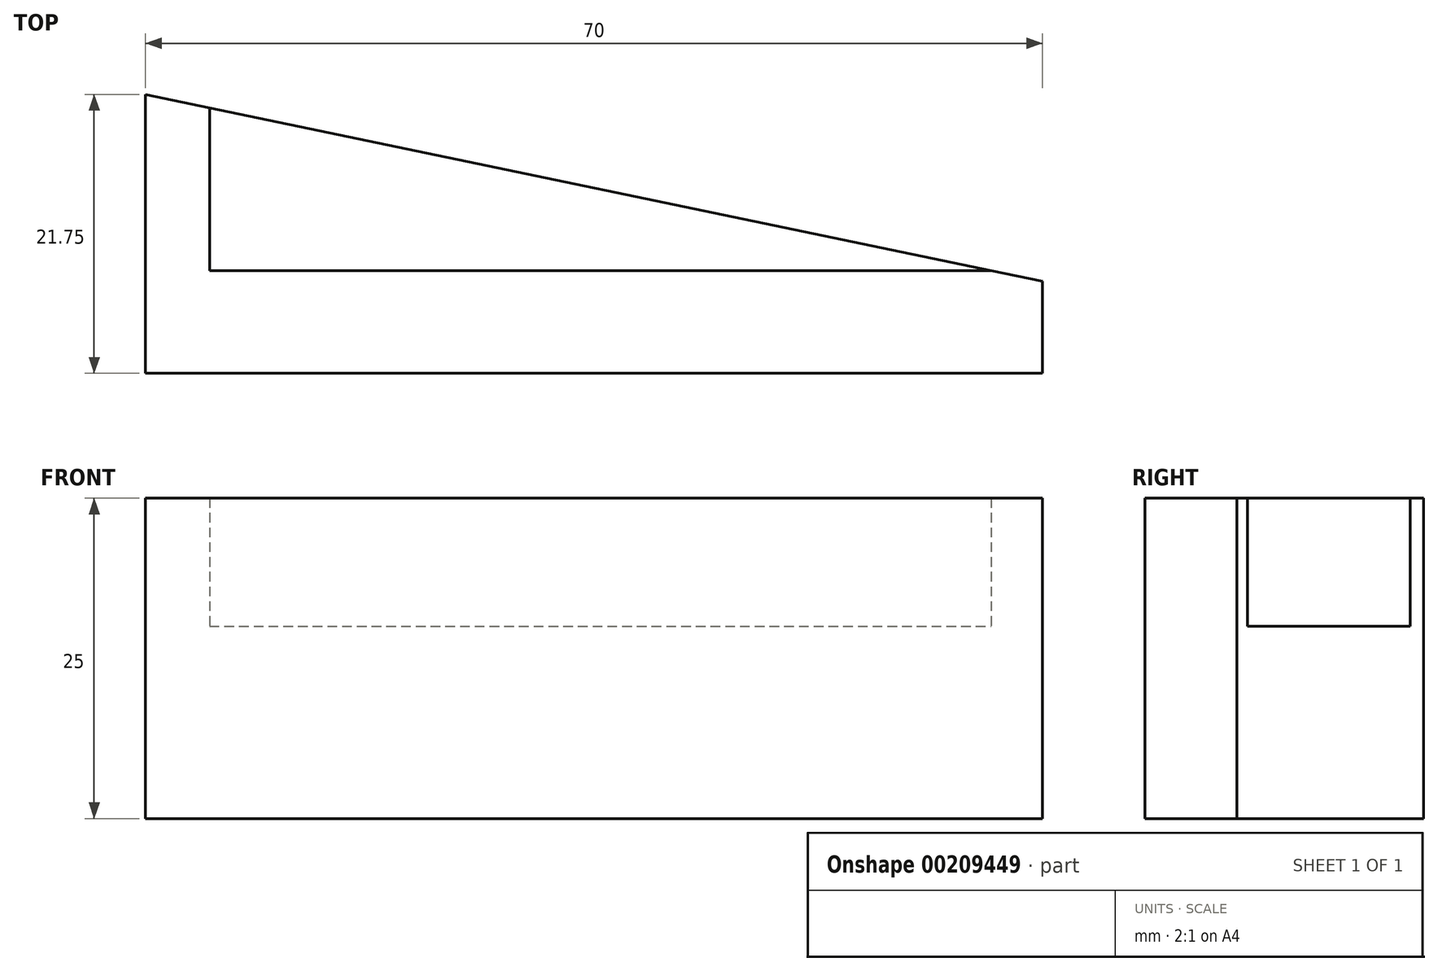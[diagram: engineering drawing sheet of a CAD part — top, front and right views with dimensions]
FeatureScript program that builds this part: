
annotation { "Feature Type Name" : "Feature", "Feature Type Description" : "" }
export const myFeature = defineFeature(function(context is Context, id is Id, definition is map)
    precondition{}
    {
        {
            var Q0;
            Q0=qCreatedBy(makeId("Top.planeOp"),FACE);
            var sketch = newSketch(context, id + "F0", { "sketchPlane" : qUnion([Q0])});
            skLineSegment(sketch, "E0", {"start": v(0, 0) * mm, "end": v(60, 0) * mm});
            skLineSegment(sketch, "E1", {"start": v(60, 0) * mm, "end": v(90, 0) * mm});
            skLineSegment(sketch, "E2", {"start": v(90, 0) * mm, "end": v(90, 18.75) * mm});
            skLineSegment(sketch, "E3", {"start": v(60, 0) * mm, "end": v(60, 12.5) * mm});
            skLineSegment(sketch, "E4", {"start": v(0, 0) * mm, "end": v(90, 18.75) * mm});
            skSolve(sketch);
        }
        {
            var Q0;
            Q0=qSketchRegion(id+"F0",true);
            extrude(context, id + "F1", {"entities" : qUnion([Q0]), "depth" : 15 * mm});
        }
        {
            var Q0;
            Q0=makeQuery(id+"F1.opExtrude","CAP_FACE",FACE,{"disambiguationData":[OSD([sQuery(id+"F0.wireOp",EDGE,"E0"),sQuery(id+"F0.wireOp",EDGE,"HZKhCLW9-oDJk-jZ79-Cc5a-FlSk4M4CYGuW"),sQuery(id+"F0.wireOp",EDGE,"E1"),sQuery(id+"F0.wireOp",EDGE,"E2")])],"isStart":false});
            var sketch = newSketch(context, id + "F2", { "sketchPlane" : qUnion([Q0])});
            skLineSegment(sketch, "E5", {"start": v(90, 0) * mm, "end": v(90, 0) * mm});
            skLineSegment(sketch, "E6", {"start": v(90, 0) * mm, "end": v(0, 0) * mm});
            skLineSegment(sketch, "E7", {"start": v(90, 0) * mm, "end": v(90, 18.75) * mm});
            skLineSegment(sketch, "E8", {"start": v(90, 18.75) * mm, "end": v(85, 17.7) * mm});
            skLineSegment(sketch, "E9.0", {"start": v(85, 5) * mm, "end": v(85, 17.7) * mm});
            skLineSegment(sketch, "E10.0", {"start": v(85, 5) * mm, "end": v(24, 5) * mm});
            skLineSegment(sketch, "E11.trimOffspring", {"start": v(24, 5) * mm, "end": v(0, 0) * mm});
            skSolve(sketch);
        }
        {
            var Q0;
            Q0=qSketchRegion(id+"F2",true);
            extrude(context, id + "F3", {"entities" : qUnion([Q0]), "operationType" : NewBodyOperationType.ADD, "depth" : 10 * mm});
        }
        {
            var Q0;
            Q0=makeQuery(id+"F1.opExtrude","SWEPT_BODY",BODY,{"disambiguationData":[OSD([sQuery(id+"F0.wireOp",EDGE,"E0"),sQuery(id+"F0.wireOp",EDGE,"E1"),sQuery(id+"F0.wireOp",EDGE,"E2"),sQuery(id+"F0.wireOp",EDGE,"E4")])]});
            var Q1;
            Q1=qCreatedBy(makeId("Right.planeOp"),FACE);
            mirror(context, id + "F4", {"entities" : qUnion([Q0]), "mirrorPlane" : qUnion([Q1])});
        }
        {
            var Q0;
            Q0=makeQuery(id+"F1.opExtrude","SWEPT_BODY",BODY,{"disambiguationData":[OSD([sQuery(id+"F0.wireOp",EDGE,"E0"),sQuery(id+"F0.wireOp",EDGE,"E1"),sQuery(id+"F0.wireOp",EDGE,"E2"),sQuery(id+"F0.wireOp",EDGE,"E4")])]});
            deleteBodies(context, id + "F5", {"entities" : qUnion([Q0])});
        }
        {
            var Q0;
            Q0=makeQuery(id+"F4.opPattern","COPY",FACE,{"derivedFrom":makeQuery(id+"F3.boolean.opBoolean","MERGE",FACE,{"derivedFrom":[makeQuery(id+"F1.opExtrude","SWEPT_FACE",FACE,{"disambiguationData":[OSD([sQuery(id+"F0.wireOp",EDGE,"E0"),sQuery(id+"F0.wireOp",EDGE,"E1")])]}),makeQuery(id+"F3.opExtrude","SWEPT_FACE",FACE,{"disambiguationData":[OSD([sQuery(id+"F2.wireOp",EDGE,"E6")])]})]}),"instanceName":"1"});
            extrude(context, id + "F6", {"entities" : qUnion([Q0]), "operationType" : NewBodyOperationType.ADD, "depth" : 3 * mm});
        }
        {
            var Q0;
            {var subQ0=sQuery(id+"F2.wireOp",EDGE,"E6");Q0=makeQuery(id+"F6.boolean.opBoolean","MERGE",FACE,{"derivedFrom":[makeQuery(id+"F4.opPattern","COPY",FACE,{"derivedFrom":makeQuery(id+"F3.opExtrude","CAP_FACE",FACE,{"disambiguationData":[OSD([subQ0,sQuery(id+"F2.wireOp",EDGE,"E7"),sQuery(id+"F2.wireOp",EDGE,"E8"),sQuery(id+"F2.wireOp",EDGE,"E9.0"),sQuery(id+"F2.wireOp",EDGE,"E10.0"),sQuery(id+"F2.wireOp",EDGE,"E11.trimOffspring")])],"isStart":false}),"instanceName":"1"}),makeQuery(id+"F6.opExtrude","SWEPT_FACE",FACE,{"disambiguationData":[OSD([subQ0])]})]});}
            var sketch = newSketch(context, id + "F7", { "sketchPlane" : qUnion([Q0])});
            skLineSegment(sketch, "E12.0", {"start": v(0, -3) * mm, "end": v(0, 0) * mm});
            skLineSegment(sketch, "E13.0", {"start": v(0, 0) * mm, "end": v(-24, 5) * mm});
            skLineSegment(sketch, "E14.0", {"start": v(-20, -3) * mm, "end": v(-20, 4.17) * mm});
            skLineSegment(sketch, "E15", {"start": v(-20, -3) * mm, "end": v(0, -3) * mm});
            skSolve(sketch);
        }
        {
            var Q0;
            Q0 = qSketchRegion(id + "F7", true);
            extrude(context, id + "F8", {"entities" : qUnion([Q0]), "operationType" : NewBodyOperationType.REMOVE, "endBound" : BoundingType.UP_TO_NEXT, "oppositeDirection" : true, "depth" : 25 * mm});
        }
    });
